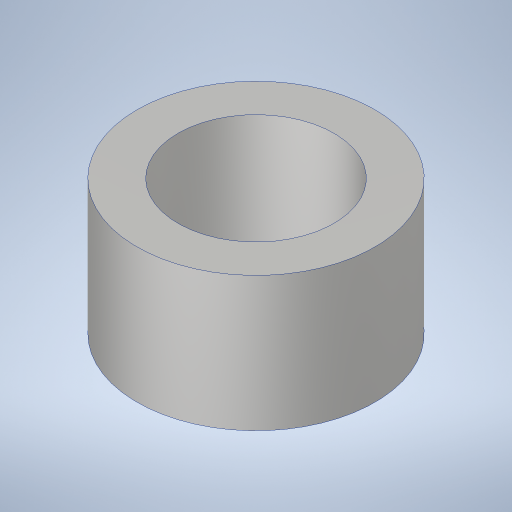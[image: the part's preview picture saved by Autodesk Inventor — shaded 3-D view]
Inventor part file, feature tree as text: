
AUTODESK INVENTOR PART (.ipt)
format: ipt  version: 2023.4 (Build 274418000, 418)  size: 212,480 bytes
history: native  units: in
note: dims shown in document units (in); Inventor stores cm internally (conversion verified against a paired STEP export)
features: extrude x1, sketch x1
ambient origin geometry x8: Origin, YZ Plane, XZ Plane, XY Plane, X Axis, Y Axis, Z Axis, Center Point
bodies: Solid1 (feature_tree)
feature tree (2):
  extrude  "Extrusion1"  Depth=0.444in
  sketch  "Sketch1"  dims[d0=0.785in d1=0.135in d2=0.444in d3=0.0in]
